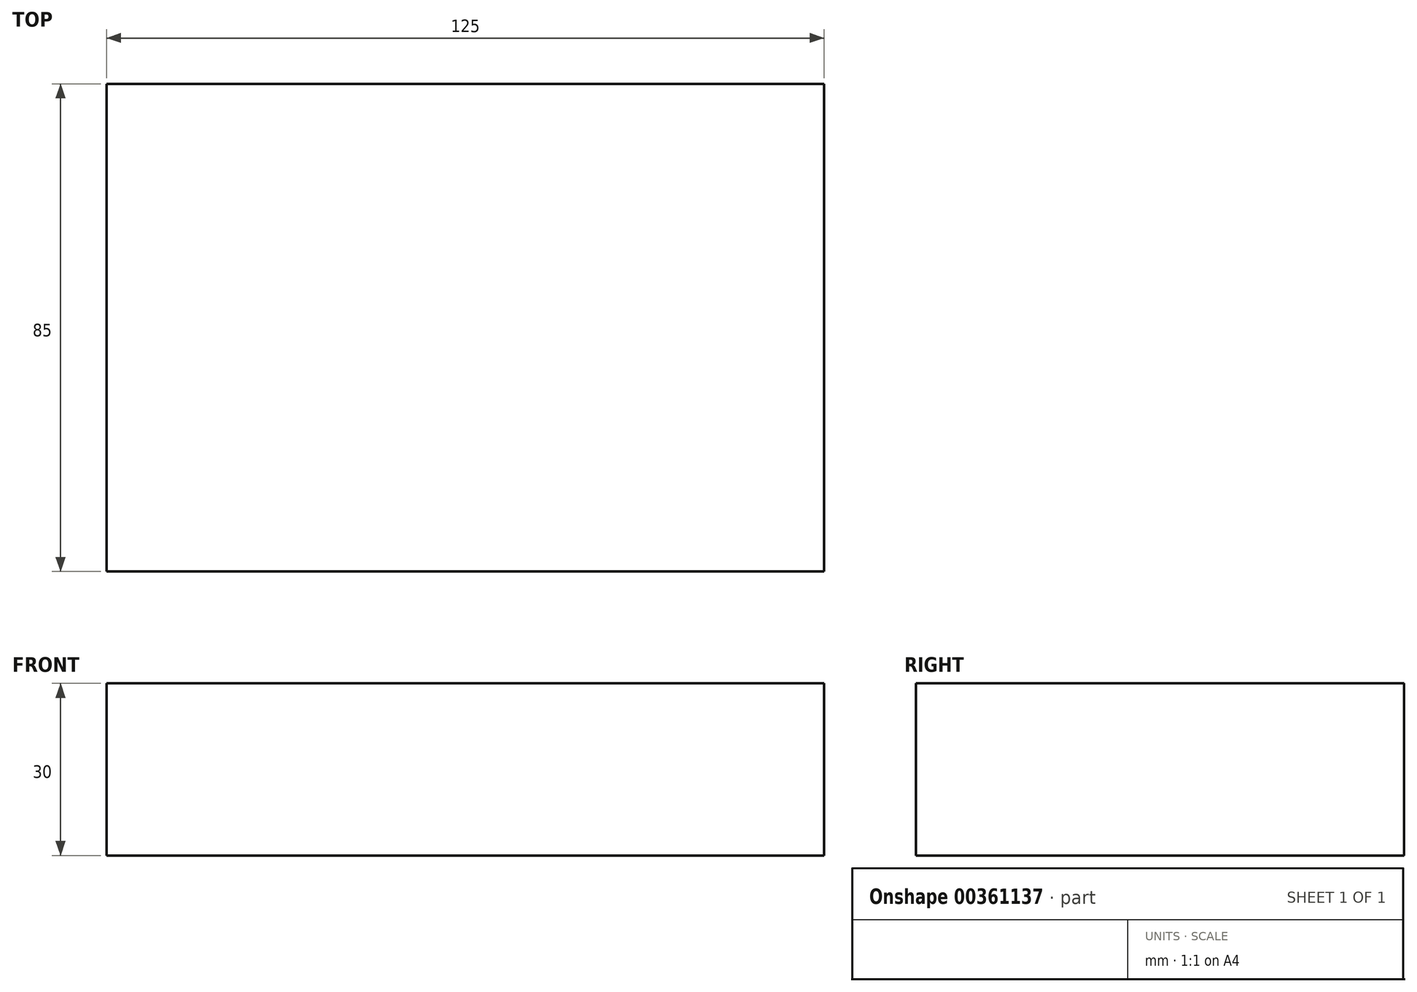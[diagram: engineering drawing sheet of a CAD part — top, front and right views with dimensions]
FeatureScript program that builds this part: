
annotation { "Feature Type Name" : "Feature", "Feature Type Description" : "" }
export const myFeature = defineFeature(function(context is Context, id is Id, definition is map)
    precondition{}
    {
        {
            var Q0;
            Q0=qCreatedBy(makeId("Top.planeOp"),FACE);
            var sketch = newSketch(context, id + "F0", { "sketchPlane" : qUnion([Q0])});
            skLineSegment(sketch, "E0.bottom", {"start": v(-62.5, 42.5) * mm, "end": v(62.5, 42.5) * mm});
            skLineSegment(sketch, "E0.top", {"start": v(-62.5, -42.5) * mm, "end": v(62.5, -42.5) * mm});
            skLineSegment(sketch, "E0.left", {"start": v(-62.5, 42.5) * mm, "end": v(-62.5, -42.5) * mm});
            skLineSegment(sketch, "E0.right", {"start": v(62.5, 42.5) * mm, "end": v(62.5, -42.5) * mm});
            skSolve(sketch);
        }
        {
            var Q0;
            Q0=makeQuery(id+"F0.imprint","IMPRINT",FACE,{"disambiguationData":[TD([[makeQuery(id+"F0.imprint","IMPRINT",EDGE,{"derivedFrom":sQuery(id+"F0.wireOp",EDGE,"E0.bottom")}),-1.0]])]});
            extrude(context, id + "F1", {"entities" : qUnion([Q0]), "endBound" : BoundingType.SYMMETRIC, "depth" : 30 * mm});
        }
    });
